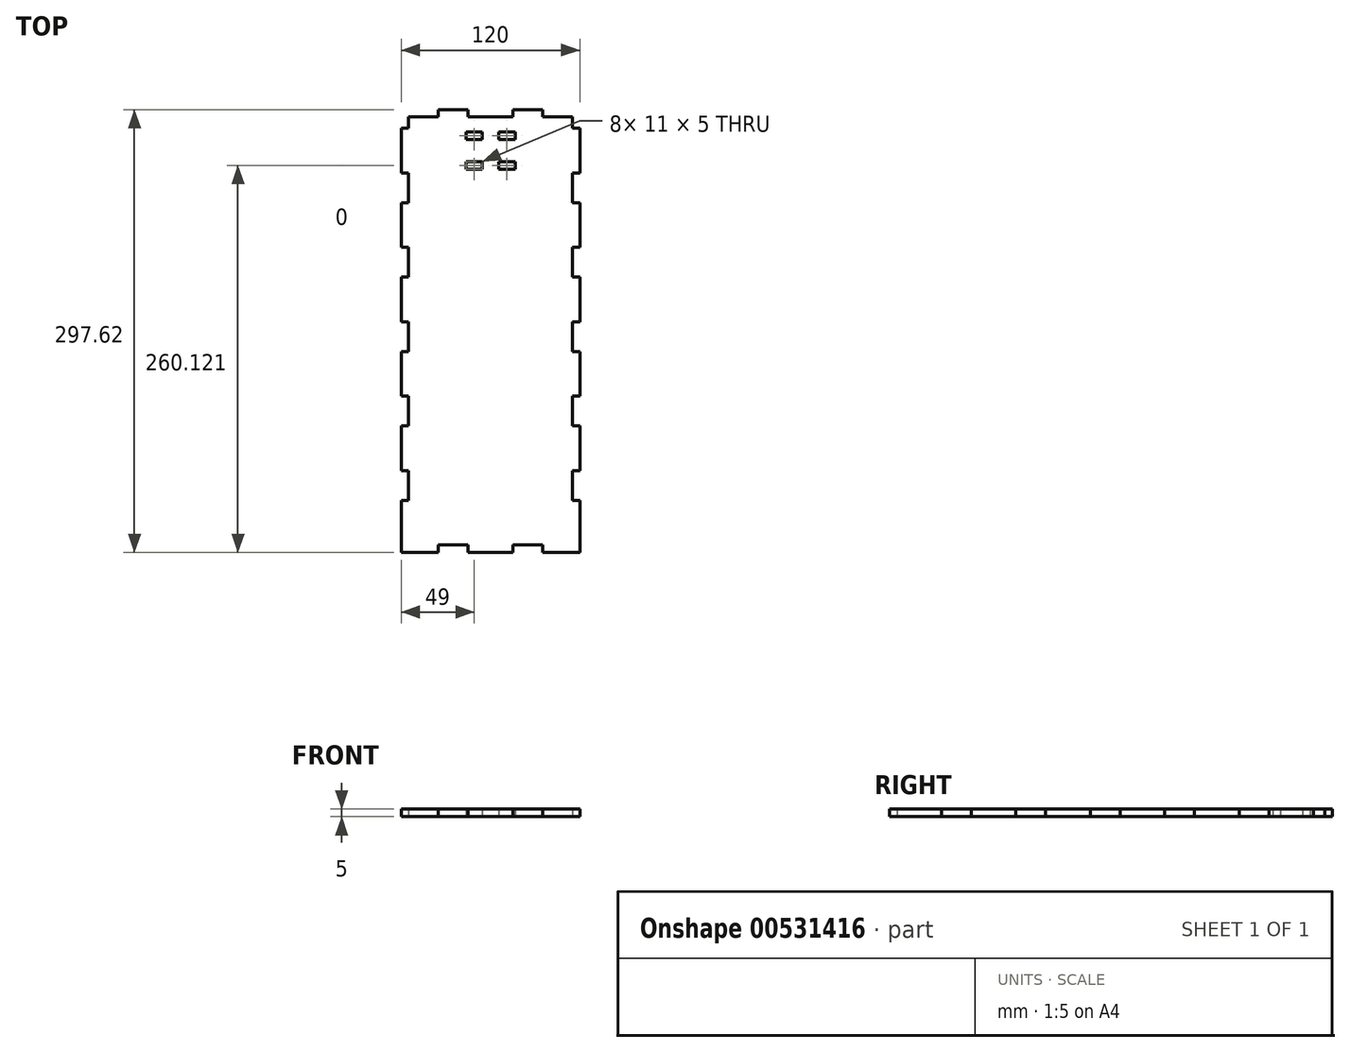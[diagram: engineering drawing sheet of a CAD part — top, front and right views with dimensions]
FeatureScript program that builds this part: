
annotation { "Feature Type Name" : "Feature", "Feature Type Description" : "" }
export const myFeature = defineFeature(function(context is Context, id is Id, definition is map)
    precondition{}
    {
        {
            var Q0;
            Q0=qCreatedBy(makeId("Top.planeOp"),FACE);
            var sketch = newSketch(context, id + "F0", { "sketchPlane" : qUnion([Q0])});
            skLineSegment(sketch, "E0.bottom", {"start": v(60, 148.81) * mm, "end": v(-60, 148.81) * mm, "construction": true});
            skLineSegment(sketch, "E0.top", {"start": v(60, -148.81) * mm, "end": v(-60, -148.81) * mm, "construction": true});
            skLineSegment(sketch, "E0.left", {"start": v(60, 148.81) * mm, "end": v(60, -148.81) * mm, "construction": true});
            skLineSegment(sketch, "E0.right", {"start": v(-60, 148.81) * mm, "end": v(-60, -148.81) * mm, "construction": true});
            skPoint(sketch, "E0.middle", {"position": v(0, 0) * mm});
            skLineSegment(sketch, "E1.bottom", {"start": v(55, 143.81) * mm, "end": v(35, 143.81) * mm});
            skLineSegment(sketch, "E1.top", {"start": v(35, -143.81) * mm, "end": v(15, -143.81) * mm});
            skLineSegment(sketch, "E1.left", {"start": v(55, 143.81) * mm, "end": v(55, 136.19) * mm});
            skLineSegment(sketch, "E1.right", {"start": v(-55, 143.81) * mm, "end": v(-55, 136.19) * mm});
            skLineSegment(sketch, "E2", {"start": v(35, -143.81) * mm, "end": v(35, -148.81) * mm});
            skLineSegment(sketch, "E3", {"start": v(35, -148.81) * mm, "end": v(60, -148.81) * mm});
            skLineSegment(sketch, "E4", {"start": v(60, -148.81) * mm, "end": v(60, -113.81) * mm});
            skLineSegment(sketch, "E5", {"start": v(60, -113.81) * mm, "end": v(55, -113.81) * mm});
            skLineSegment(sketch, "E6", {"start": v(15, -143.81) * mm, "end": v(15, -148.81) * mm});
            skLineSegment(sketch, "E7.MirrorCS", {"start": v(-15, -143.81) * mm, "end": v(-15, -148.81) * mm});
            skLineSegment(sketch, "E8.MirrorCS", {"start": v(-35, -143.81) * mm, "end": v(-35, -148.81) * mm});
            skLineSegment(sketch, "E9.MirrorCS", {"start": v(-60, -113.81) * mm, "end": v(-55, -113.81) * mm});
            skLineSegment(sketch, "E10", {"start": v(-15, -148.81) * mm, "end": v(15, -148.81) * mm});
            skLineSegment(sketch, "E11", {"start": v(-35, -148.81) * mm, "end": v(-60, -148.81) * mm});
            skLineSegment(sketch, "E12", {"start": v(-60, -113.81) * mm, "end": v(-60, -148.81) * mm});
            skPoint(sketch, "E13.orphan", {"position": v(-55, -143.81) * mm});
            skLineSegment(sketch, "E14.trimOffspring", {"start": v(-15, -143.81) * mm, "end": v(-35, -143.81) * mm});
            skPoint(sketch, "E15.orphan", {"position": v(55, -143.81) * mm});
            skLineSegment(sketch, "E16", {"start": v(55, -93.81) * mm, "end": v(60, -93.81) * mm});
            skLineSegment(sketch, "E17", {"start": v(60, -93.81) * mm, "end": v(60, -63.81) * mm});
            skLineSegment(sketch, "E18", {"start": v(60, -63.81) * mm, "end": v(55, -63.81) * mm});
            skLineSegment(sketch, "E19", {"start": v(55, -63.81) * mm, "end": v(55, -43.81) * mm});
            skLineSegment(sketch, "E20", {"start": v(55, -43.81) * mm, "end": v(60, -43.81) * mm});
            skLineSegment(sketch, "E21", {"start": v(60, -43.81) * mm, "end": v(60, -13.81) * mm});
            skLineSegment(sketch, "E22", {"start": v(60, -13.81) * mm, "end": v(55, -13.81) * mm});
            skLineSegment(sketch, "E23", {"start": v(60, 6.19) * mm, "end": v(55, 6.19) * mm});
            skPoint(sketch, "E23.endSnap0", {"position": v(55, 15) * mm});
            skLineSegment(sketch, "E24", {"start": v(60, 6.19) * mm, "end": v(60, 36.19) * mm});
            skLineSegment(sketch, "E25", {"start": v(60, 36.19) * mm, "end": v(55, 36.19) * mm});
            skLineSegment(sketch, "E26", {"start": v(55, 36.19) * mm, "end": v(55, 56.19) * mm});
            skLineSegment(sketch, "E27", {"start": v(55, 56.19) * mm, "end": v(60, 56.19) * mm});
            skLineSegment(sketch, "E28", {"start": v(60, 56.19) * mm, "end": v(60, 86.19) * mm});
            skLineSegment(sketch, "E29", {"start": v(60, 86.19) * mm, "end": v(55, 86.19) * mm});
            skLineSegment(sketch, "E30", {"start": v(55, 86.19) * mm, "end": v(55, 106.19) * mm});
            skLineSegment(sketch, "E31", {"start": v(55, 106.19) * mm, "end": v(60, 106.19) * mm});
            skLineSegment(sketch, "E32", {"start": v(60, 106.19) * mm, "end": v(60, 136.19) * mm});
            skLineSegment(sketch, "E33", {"start": v(60, 136.19) * mm, "end": v(55, 136.19) * mm});
            skLineSegment(sketch, "E34.MirrorCS", {"start": v(-60, 136.19) * mm, "end": v(-55, 136.19) * mm});
            skLineSegment(sketch, "E35.MirrorCS", {"start": v(-55, 106.19) * mm, "end": v(-60, 106.19) * mm});
            skLineSegment(sketch, "E36.MirrorCS", {"start": v(-60, 86.19) * mm, "end": v(-55, 86.19) * mm});
            skLineSegment(sketch, "E37.MirrorCS", {"start": v(-55, 56.19) * mm, "end": v(-60, 56.19) * mm});
            skLineSegment(sketch, "E38.MirrorCS", {"start": v(-60, 36.19) * mm, "end": v(-55, 36.19) * mm});
            skLineSegment(sketch, "E39.MirrorCS", {"start": v(-60, 6.19) * mm, "end": v(-55, 6.19) * mm});
            skLineSegment(sketch, "E40.MirrorCS", {"start": v(-60, -13.81) * mm, "end": v(-55, -13.81) * mm});
            skLineSegment(sketch, "E41.MirrorCS", {"start": v(-55, -43.81) * mm, "end": v(-60, -43.81) * mm});
            skLineSegment(sketch, "E42.MirrorCS", {"start": v(-60, -63.81) * mm, "end": v(-55, -63.81) * mm});
            skLineSegment(sketch, "E43.MirrorCS", {"start": v(-55, -93.81) * mm, "end": v(-60, -93.81) * mm});
            skLineSegment(sketch, "E44", {"start": v(-60, -93.81) * mm, "end": v(-60, -63.81) * mm});
            skLineSegment(sketch, "E45", {"start": v(-60, -43.81) * mm, "end": v(-60, -13.81) * mm});
            skLineSegment(sketch, "E46", {"start": v(-60, 6.19) * mm, "end": v(-60, 36.19) * mm});
            skLineSegment(sketch, "E47", {"start": v(-60, 56.19) * mm, "end": v(-60, 86.19) * mm});
            skLineSegment(sketch, "E48", {"start": v(-60, 106.19) * mm, "end": v(-60, 136.19) * mm});
            skLineSegment(sketch, "E49.trimOffspring", {"start": v(-55, 106.19) * mm, "end": v(-55, 86.19) * mm});
            skLineSegment(sketch, "E50.trimOffspring", {"start": v(-55, 56.19) * mm, "end": v(-55, 36.19) * mm});
            skLineSegment(sketch, "E51.trimOffspring", {"start": v(-55, 6.19) * mm, "end": v(-55, -13.81) * mm});
            skLineSegment(sketch, "E52.trimOffspring", {"start": v(-55, -43.81) * mm, "end": v(-55, -63.81) * mm});
            skLineSegment(sketch, "E53.trimOffspring", {"start": v(-55, -93.81) * mm, "end": v(-55, -113.81) * mm});
            skLineSegment(sketch, "E54.trimOffspring", {"start": v(55, -93.81) * mm, "end": v(55, -113.81) * mm});
            skLineSegment(sketch, "E55.trimOffspring", {"start": v(55, -43.81) * mm, "end": v(55, -63.81) * mm});
            skLineSegment(sketch, "E56.trimOffspring", {"start": v(55, 6.19) * mm, "end": v(55, -13.81) * mm});
            skLineSegment(sketch, "E57.trimOffspring", {"start": v(55, 56.19) * mm, "end": v(55, 36.19) * mm});
            skLineSegment(sketch, "E58.trimOffspring", {"start": v(55, 106.19) * mm, "end": v(55, 86.19) * mm});
            skLineSegment(sketch, "E59", {"start": v(35, 143.81) * mm, "end": v(35, 148.81) * mm});
            skLineSegment(sketch, "E60", {"start": v(35, 148.81) * mm, "end": v(15, 148.81) * mm});
            skLineSegment(sketch, "E61", {"start": v(15, 148.81) * mm, "end": v(15, 143.81) * mm});
            skLineSegment(sketch, "E62", {"start": v(15, 143.81) * mm, "end": v(-15, 143.81) * mm});
            skLineSegment(sketch, "E63", {"start": v(-15, 143.81) * mm, "end": v(-15, 148.81) * mm});
            skLineSegment(sketch, "E64", {"start": v(-15, 148.81) * mm, "end": v(-35, 148.81) * mm});
            skLineSegment(sketch, "E65", {"start": v(-35, 148.81) * mm, "end": v(-35, 143.81) * mm});
            skLineSegment(sketch, "E66.bottom", {"start": v(-16.5, 113.81) * mm, "end": v(-5.5, 113.81) * mm});
            skLineSegment(sketch, "E66.top", {"start": v(-16.5, 108.81) * mm, "end": v(-5.5, 108.81) * mm});
            skLineSegment(sketch, "E66.left", {"start": v(-16.5, 113.81) * mm, "end": v(-16.5, 108.81) * mm});
            skLineSegment(sketch, "E66.right", {"start": v(-5.5, 113.81) * mm, "end": v(-5.5, 108.81) * mm});
            skLineSegment(sketch, "E67.MirrorCS", {"start": v(16.5, 113.81) * mm, "end": v(5.5, 113.81) * mm});
            skLineSegment(sketch, "E68.MirrorCS", {"start": v(16.5, 108.81) * mm, "end": v(5.5, 108.81) * mm});
            skLineSegment(sketch, "E69.MirrorCS", {"start": v(16.5, 113.81) * mm, "end": v(16.5, 108.81) * mm});
            skLineSegment(sketch, "E70.MirrorCS", {"start": v(5.5, 113.81) * mm, "end": v(5.5, 108.81) * mm});
            skLineSegment(sketch, "E71", {"start": v(-16.5, 121.31) * mm, "end": v(16.5, 121.31) * mm, "construction": true});
            skLineSegment(sketch, "E72.MirrorCS", {"start": v(-16.5, 128.81) * mm, "end": v(-5.5, 128.81) * mm});
            skLineSegment(sketch, "E73.MirrorCS", {"start": v(-16.5, 133.81) * mm, "end": v(-5.5, 133.81) * mm});
            skLineSegment(sketch, "E74.MirrorCS", {"start": v(-16.5, 128.81) * mm, "end": v(-16.5, 133.81) * mm});
            skLineSegment(sketch, "E75.MirrorCS", {"start": v(-5.5, 128.81) * mm, "end": v(-5.5, 133.81) * mm});
            skLineSegment(sketch, "E76.MirrorCS", {"start": v(5.5, 128.81) * mm, "end": v(5.5, 133.81) * mm});
            skLineSegment(sketch, "E77.MirrorCS", {"start": v(16.5, 128.81) * mm, "end": v(5.5, 128.81) * mm});
            skLineSegment(sketch, "E78.MirrorCS", {"start": v(16.5, 128.81) * mm, "end": v(16.5, 133.81) * mm});
            skLineSegment(sketch, "E79.MirrorCS", {"start": v(16.5, 133.81) * mm, "end": v(5.5, 133.81) * mm});
            skLineSegment(sketch, "E80.trimOffspring", {"start": v(-35, 143.81) * mm, "end": v(-55, 143.81) * mm});
            skSolve(sketch);
        }
        {
            var Q0;
            Q0 = qSketchRegion(id + "F0", true);
            extrude(context, id + "F1", {"entities" : qUnion([Q0]), "depth" : 5 * mm, "offsetDistance" : 25 * mm});
        }
    });
